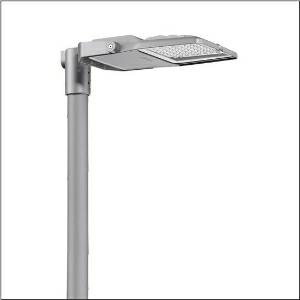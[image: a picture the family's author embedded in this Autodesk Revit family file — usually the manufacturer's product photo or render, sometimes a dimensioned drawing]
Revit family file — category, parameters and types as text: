
# Revit family: floodlight_fl_21_mini___pl64_5xa7776d2e3a_9c1a
name_source: partatom
category: Lighting Fixtures
units: mm (PartAtom-declared; Revit-internal decimal feet)

## family parameters
Cut with Voids When Loaded = No
Host = Face
Light Source = No
Part Type = Normal
Room Calculation Point = No
Round Connector Dimension = Use Diameter
Shared = No

## types (1)
- --- (1 x LED, 17220 lm, 142.9 W, 3000K)
    Apparent Load = 143 VA
    CIE Flux Codes = 28 80 98 100 100
    Color Rendering = 70
    Color Temperature = 3000K
    Default Elevation = 1800 mm
    Description = Floodlight FL 21 mini, floodlight, primary light control with lens, of PMMA, primary optical cover: protective disc, of toughened safety glass, transparent, light distribution: PL64, light emission: direct distribution, installation type: surface-mounted, LED, High Power LED, rated luminous flux: 17.220lm, luminous efficacy: 121lm/W, light colour: 730, colour temperature: 3000K, control gear: Smart Interface (Zhaga), control: flexible luminous flux parameterisation, time-dependent luminous flux control, constant luminous flux control, overheat protection, pre-setting: logarithmic dimming characteristic, with terminal, 6-pole, mains connection: 220..240V, AC, 50/60Hz, start of lifetime: 143W, end of service life: 151W, reduction: 63W, luminaire housing, of diecast aluminium, powder-coated, Siteco® metallic grey (DB 702S), corrosivity category C5 mid according to DIN EN ISO 12944, suitable for swimming pools, chlorine-resistant, sealing non-destructively replaceable, please order mast flange separately, mast bracket, of steel, galvanised, powder-coated, Siteco® metallic grey (DB 702S), Smart Interface below and above, protection rating (complete): IP66, insulation class (complete): insulation class II (safety insulation), certification: CE, ENEC, VDE, protection symbol: D, impact resistance: IK08, permissible operating ambient temperature: -40..+40°C, permissible operating ambient temperature for outdoor applications: -40..+50°C, standard: DIN EN 12944, LABS conformity tested according to VDMA 24364:2018-05, packaging unit: 1 piece

Light Distribution: PL64
    Height = 70 mm
    Lamp = 1 x LED
    Lamp Light Flux = 17220 lm
    Lamp Power = 142.9 W
    Lamp count = 1
    Length = 485 mm
    Luminous efficacy = 121 lm/W
    Manufacturer = Siteco
    ModVariant = No
    Model = 5XA7776D2E3A
    Number of Poles = 1
    OnlyDefault = Yes
    Power Factor = 1
    Product Name = Floodlight FL 21 mini | PL64
    Product group = floodlight | pylon annexe
    ProductGroupID = 6201
    Protection Class = Protection class II
    Protection Degree = IP 66
    RLX_Detail_Level = 1
    RLX_Emergency_Light_Flux = 0 lm
    RLX_Emergency_Type = 0
    RLX_Emergency_Type_DB = No
    RlxData = <blob elided: 101405 chars, md5=8834efec>
    Socket = socket
    Standby Power = 0 W
    System Light Flux = 17220 lm
    System Power = 143 W
    Type Comments = factory setting: luminous flux: 100 % | dim-lin: 254 | 730 mA
    Type Image = l_1007125.jpg
    URL = http://relux.com
    VarID = @adj_186661
    Voltage = 0 V
    Weight = 0.00 kg
    Width = 337 mm

## geometry (parser evidence)
native form markers: Blend x4, Sweep x14
no freeform markers — native parametric forms only
